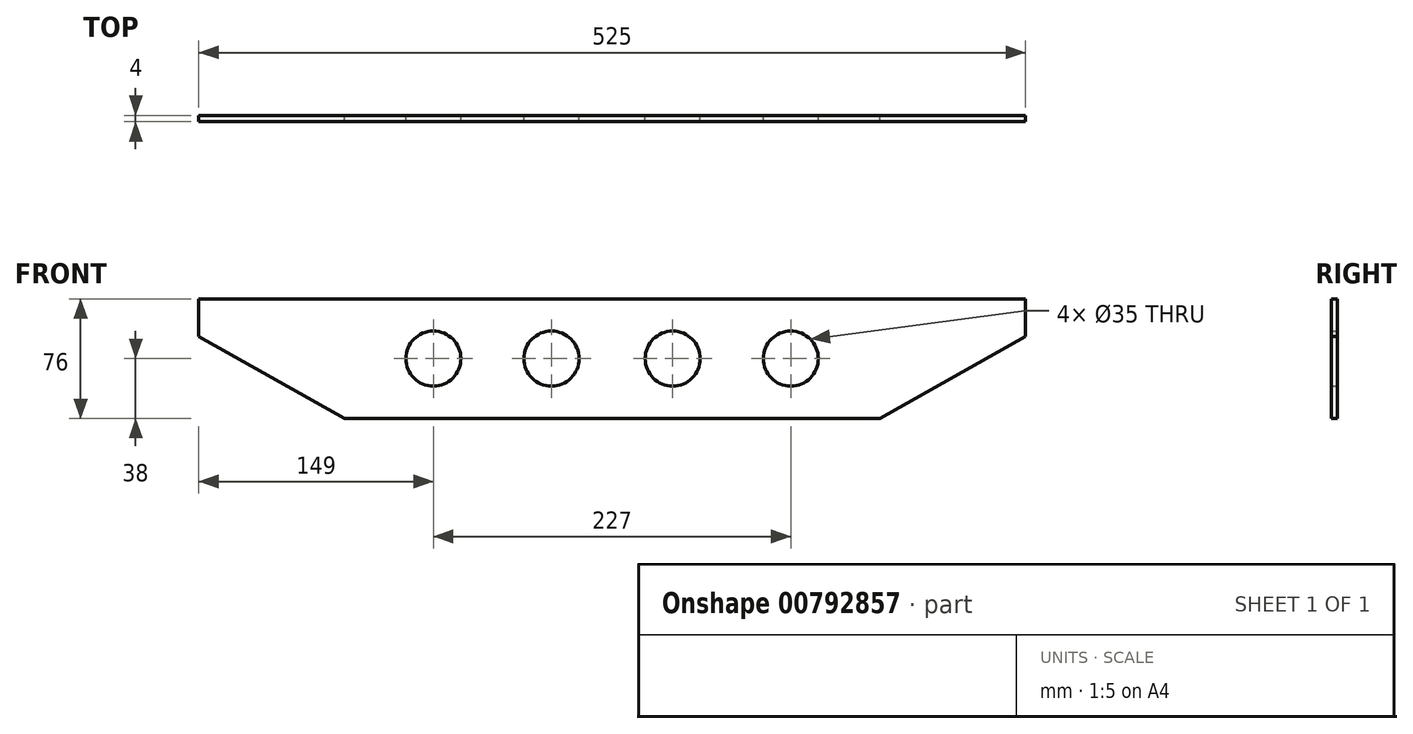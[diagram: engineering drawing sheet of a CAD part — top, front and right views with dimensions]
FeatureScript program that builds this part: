
annotation { "Feature Type Name" : "Feature", "Feature Type Description" : "" }
export const myFeature = defineFeature(function(context is Context, id is Id, definition is map)
    precondition{}
    {
        {
            var Q0;
            Q0=qCreatedBy(makeId("Front.planeOp"),FACE);
            var sketch = newSketch(context, id + "F0", { "sketchPlane" : qUnion([Q0])});
            skLineSegment(sketch, "E0", {"start": v(0, 380.62) * mm, "end": v(0, -430.36) * mm, "construction": true});
            skLineSegment(sketch, "E1", {"start": v(494.6, 0) * mm, "end": v(-569.21, 0) * mm, "construction": true});
            skLineSegment(sketch, "E2", {"start": v(0, 38) * mm, "end": v(-262.5, 38) * mm});
            skLineSegment(sketch, "E3", {"start": v(-262.5, 38) * mm, "end": v(-262.5, 14) * mm});
            skLineSegment(sketch, "E4", {"start": v(0, -38) * mm, "end": v(-170, -38) * mm});
            skLineSegment(sketch, "E5", {"start": v(-262.5, 14) * mm, "end": v(-170, -38) * mm});
            skCircle(sketch, "E6", {"center": v(-113.5, 0) * mm, "radius": 17.5 * mm});
            skCircle(sketch, "E7", {"center": v(-38.5, 0) * mm, "radius": 17.5 * mm});
            skLineSegment(sketch, "E8.MirrorCS", {"start": v(0, 38) * mm, "end": v(262.5, 38) * mm});
            skLineSegment(sketch, "E9.MirrorCS", {"start": v(262.5, 38) * mm, "end": v(262.5, 14) * mm});
            skLineSegment(sketch, "E10.MirrorCS", {"start": v(262.5, 14) * mm, "end": v(170, -38) * mm});
            skLineSegment(sketch, "E11.MirrorCS", {"start": v(0, -38) * mm, "end": v(170, -38) * mm});
            skCircle(sketch, "E12.MirrorC", {"center": v(113.5, 0) * mm, "radius": 17.5 * mm});
            skCircle(sketch, "E13.MirrorC", {"center": v(38.5, 0) * mm, "radius": 17.5 * mm});
            skSolve(sketch);
        }
        {
            var Q0;
            Q0 = qSketchRegion(id + "F0", true);
            extrude(context, id + "F1", {"entities" : qUnion([Q0]), "depth" : 4 * mm, "offsetDistance" : 25 * mm});
        }
    });
